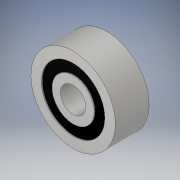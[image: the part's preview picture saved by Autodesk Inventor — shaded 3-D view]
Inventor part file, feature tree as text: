
AUTODESK INVENTOR PART (.ipt)
format: ipt  version: 2017 (Build 210142000, 142)  size: 133,632 bytes
history: native  units: in
note: dims shown in document units (in); Inventor stores cm internally (conversion verified against a paired STEP export)
features: extrude x2, sketch x2, mirror x1, projected_geometry x1
ambient origin geometry x8: Origin, YZ Plane, XZ Plane, XY Plane, X Axis, Y Axis, Z Axis, Center Point
bodies: Solid1 (feature_tree)
feature tree (6):
  extrude  "Extrusion1"  Depth=0.3937in
  extrude  "Extrusion2"  Depth=0.0039in
  mirror  "Mirror1"
  sketch  "Sketch1"  dims[d0=0.1181in d1=0.3937in]
  sketch  "Sketch2"  dims[d2=0.1575in d3=0.0in d4=0.0492in d5=0.0394in d6=0.0039in d7=0.0in]
  projected_geometry  "Projected Loop1"
